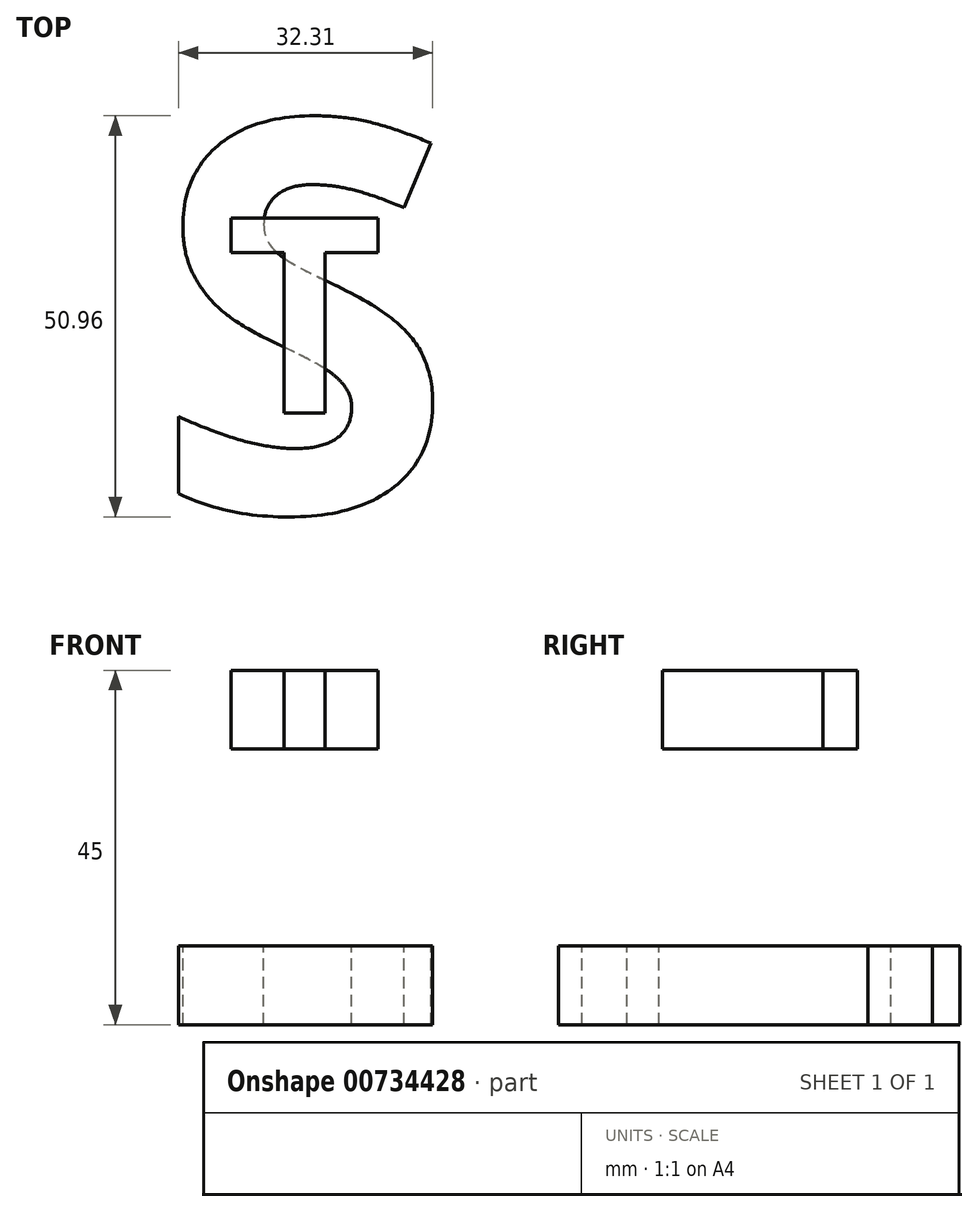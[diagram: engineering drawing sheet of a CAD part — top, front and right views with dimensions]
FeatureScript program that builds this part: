
annotation { "Feature Type Name" : "Feature", "Feature Type Description" : "" }
export const myFeature = defineFeature(function(context is Context, id is Id, definition is map)
    precondition{}
    {
        {
            var Q0;
            Q0=qCreatedBy(makeId("Top.planeOp"),FACE);
            cPlane(context, id + "F0", {"entities" : qUnion([Q0]), "cplaneType" : CPlaneType.OFFSET, "offset" : 25 * mm, "width" : 150 * mm, "height" : 150 * mm});
        }
        {
            var Q0;
            Q0=qCreatedBy(id+"F0.planeOp",FACE);
            var sketch = newSketch(context, id + "F1", { "sketchPlane" : qUnion([Q0])});
            skText(sketch, "E0", { "text": "T", "fontName": "OpenSans-Bold.ttf"});
            const initialGuessF1  = {"E0": [-0.01083, -0.0125, 1, 0, 0.025]};
            skSetInitialGuess(sketch, initialGuessF1);
            skSolve(sketch);
        }
        {
            var Q0;
            Q0=qCreatedBy(makeId("Top.planeOp"),FACE);
            var sketch = newSketch(context, id + "F2", { "sketchPlane" : qUnion([Q0])});
            skText(sketch, "E1", { "text": "S", "fontName": "OpenSans-Bold.ttf"});
            const initialGuessF2  = {"E1": [-0.02, -0.025, 1, 0, 0.05]};
            skSetInitialGuess(sketch, initialGuessF2);
            skSolve(sketch);
        }
        {
            var Q0;
            Q0 = qSketchRegion(id + "F1", true);
            extrude(context, id + "F3", {"entities" : qUnion([Q0]), "depth" : 10 * mm, "offsetDistance" : 25 * mm});
        }
        {
            var Q0;
            Q0 = qSketchRegion(id + "F2", true);
            extrude(context, id + "F4", {"entities" : qUnion([Q0]), "oppositeDirection" : true, "depth" : 10 * mm, "offsetDistance" : 25 * mm});
        }
    });
